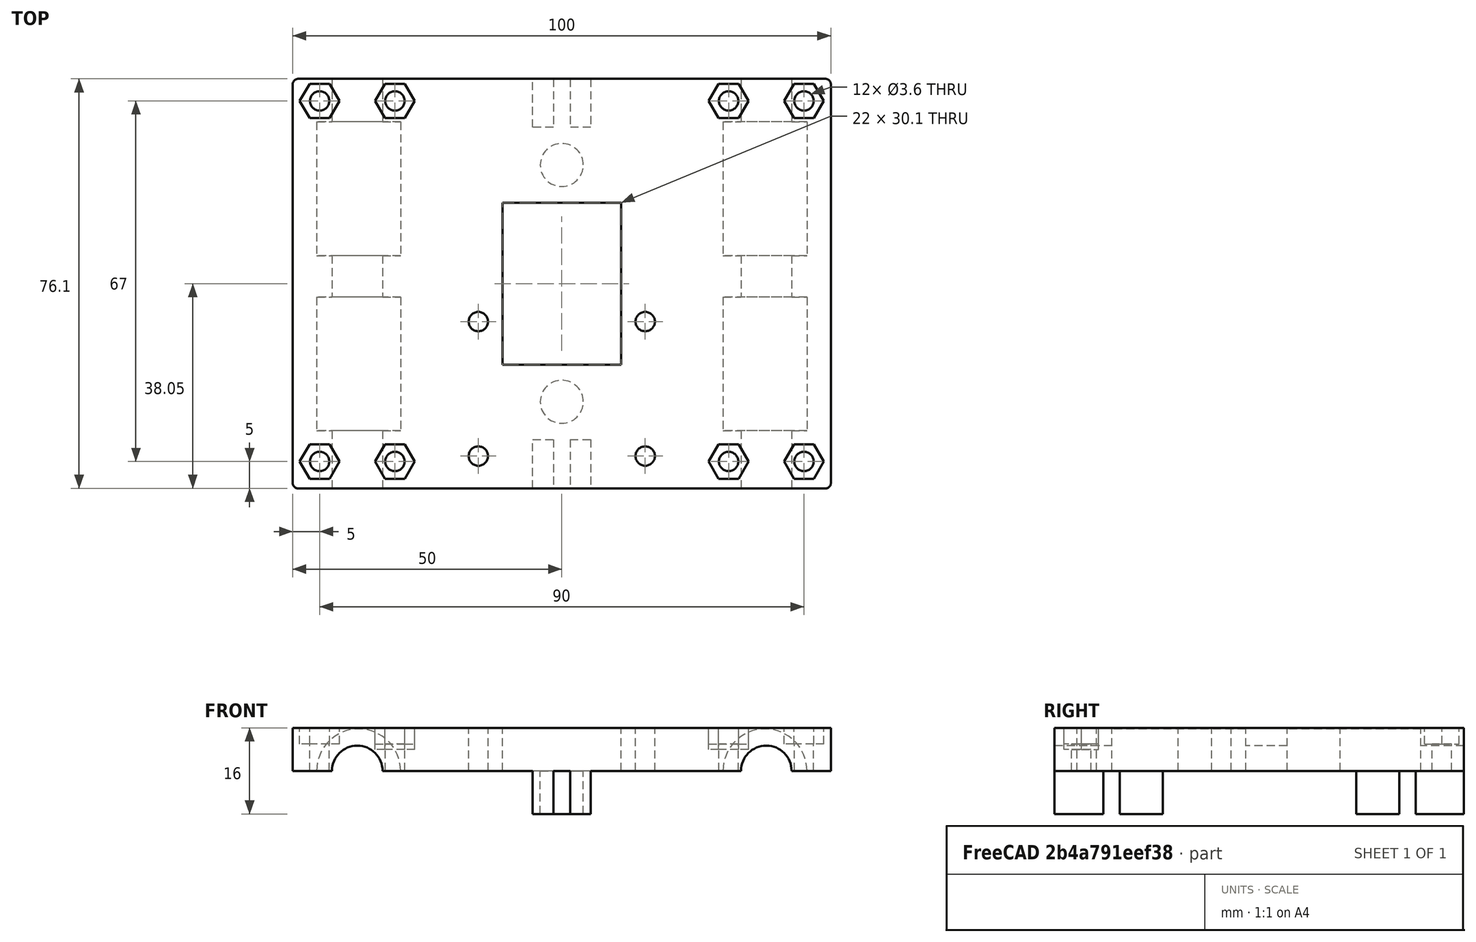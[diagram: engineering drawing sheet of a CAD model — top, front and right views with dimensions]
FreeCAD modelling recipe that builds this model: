
FCSTD DOCUMENT  (FreeCAD 0.15R4671 (Git))
Label: Soporte principal 4.0
License: All rights reserved
LicenseURL: http://en.wikipedia.org/wiki/All_rights_reserved
objects: Part::Cut×10, Part::Cylinder×6, Part::Prism×4, Part::Feature×1
note: 21 computed .brp shape members not serialized (recipe doc carries the construction recipe); baked Part::Feature solids carry a one-line shape summary decoded from their .brp

FEATURE [Part::Feature] Fillet003001  label="Soporte principal "
  shape: bbox 100 x 76.1 x 16 mm, 90 faces (baked)
FEATURE [Part::Cylinder] Cylinder037  label="Cilindro022"
  Angle = 360
  Height = 20
  Placement = pos=(81,72,-10) rot=(0,0,1;0rad)
  Radius = 1.8
FEATURE [Part::Cut] Cut010035003015  label="Soporte principal'"
  Base = -> Fillet003001
  Tool = -> Cylinder037
FEATURE [Part::Prism] Prism004  label="Prisma004"
  Circumradius = 3.7
  Height = 10
  Placement = pos=(81,72,5) rot=(0,0,1;0rad)
  Polygon = 6
FEATURE [Part::Cut] Cut010035003016  label="Soporte principal''"
  Base = -> Cut010035003015
  Tool = -> Prism004
FEATURE [Part::Cylinder] Cylinder039  label="Cilindro024"
  Angle = 360
  Height = 20
  Placement = pos=(81,5,-10) rot=(0,0,1;0rad)
  Radius = 1.8
FEATURE [Part::Cut] Cut010035003019  label="Soporte principal ''''"
  Base = -> Cut010035003016
  Tool = -> Cylinder039
FEATURE [Part::Prism] Prism006  label="Prisma006"
  Circumradius = 3.7
  Height = 10
  Placement = pos=(81,5,4) rot=(0,0,1;0rad)
  Polygon = 6
FEATURE [Part::Cut] Cut010035003021  label="Soporte principal V"
  Base = -> Cut010035003019
  Tool = -> Prism006
FEATURE [Part::Cylinder] Cylinder043  label="Cilindro028"
  Angle = 360
  Height = 20
  Placement = pos=(19,72,-10) rot=(0,0,1;0rad)
  Radius = 1.8
FEATURE [Part::Cut] Cut010035003024  label="Soporte principal V'"
  Base = -> Cut010035003021
  Tool = -> Cylinder043
FEATURE [Part::Prism] Prism007  label="Prisma007"
  Circumradius = 3.7
  Height = 10
  Placement = pos=(19,72,5) rot=(0,0,1;0rad)
  Polygon = 6
FEATURE [Part::Cut] Cut010035003025  label="Soporte principal V'''"
  Base = -> Cut010035003024
  Tool = -> Prism007
FEATURE [Part::Cylinder] Cylinder046  label="Cilindro031"
  Angle = 360
  Height = 20
  Placement = pos=(19,5,-10) rot=(0,0,1;0rad)
  Radius = 1.8
FEATURE [Part::Cut] Cut010035003028  label="Soporte principal VI"
  Base = -> Cut010035003025
  Tool = -> Cylinder046
FEATURE [Part::Prism] Prism008  label="Prisma008"
  Circumradius = 3.7
  Height = 10
  Placement = pos=(19,5,4) rot=(0,0,1;0rad)
  Polygon = 6
FEATURE [Part::Cut] Cut010035003029  label="Soporte principal VI'"
  Base = -> Cut010035003028
  Tool = -> Prism008
FEATURE [Part::Cylinder] Cylinder
  Angle = 360
  Height = 100
  Placement = pos=(12,79,0) rot=(1,0,0;1.5708rad)
  Radius = 4.7
FEATURE [Part::Cylinder] Cylinder047
  Angle = 360
  Height = 100
  Placement = pos=(88,79,0) rot=(1,0,0;1.5708rad)
  Radius = 4.7
FEATURE [Part::Cut] Cut
  Base = -> Cut010035003029
  Tool = -> Cylinder
FEATURE [Part::Cut] Cut010035003030
  Base = -> Cut
  Tool = -> Cylinder047
